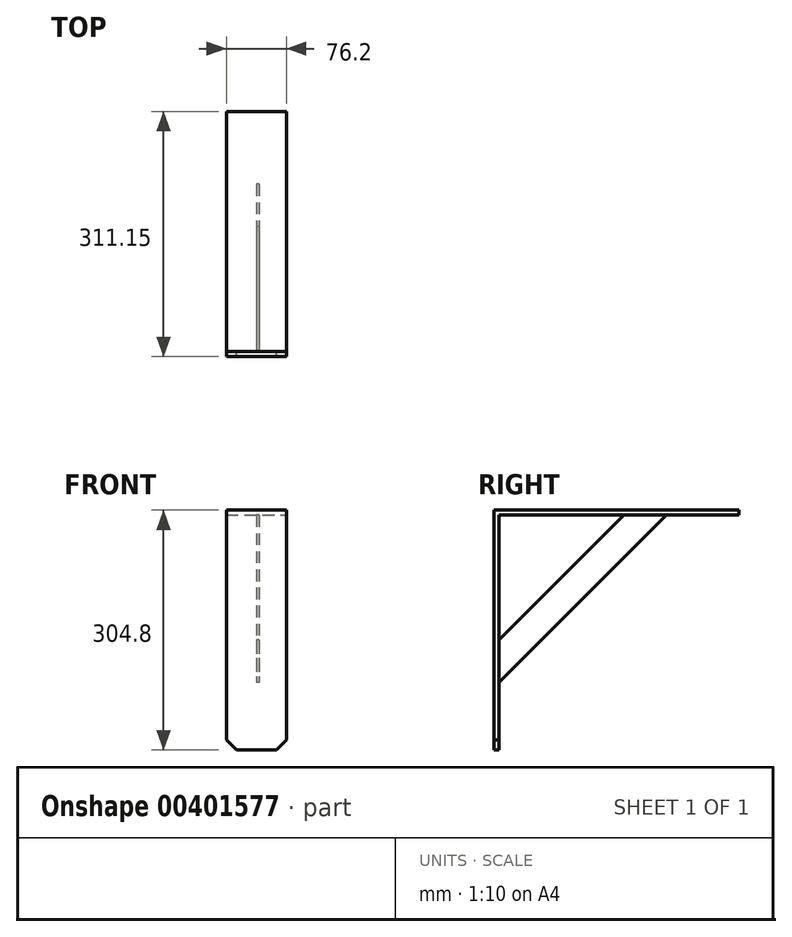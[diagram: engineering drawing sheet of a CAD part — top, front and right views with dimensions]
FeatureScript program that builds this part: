
annotation { "Feature Type Name" : "Feature", "Feature Type Description" : "" }
export const myFeature = defineFeature(function(context is Context, id is Id, definition is map)
    precondition{}
    {
        {
            var Q0;
            Q0=qCreatedBy(makeId("Front.planeOp"),FACE);
            var sketch = newSketch(context, id + "F0", { "sketchPlane" : qUnion([Q0])});
            skLineSegment(sketch, "E0.bottom", {"start": v(25.4, -152.4) * mm, "end": v(-38.1, -152.4) * mm});
            skLineSegment(sketch, "E0.top", {"start": v(38.1, 152.4) * mm, "end": v(-38.1, 152.4) * mm});
            skLineSegment(sketch, "E0.left", {"start": v(38.1, -139.7) * mm, "end": v(38.1, 152.4) * mm});
            skLineSegment(sketch, "E0.right", {"start": v(-38.1, -139.7) * mm, "end": v(-38.1, 152.4) * mm});
            skPoint(sketch, "E0.middle", {"position": v(0, 0) * mm});
            skLineSegment(sketch, "E1", {"start": v(-38.1, -139.7) * mm, "end": v(-25.4, -152.4) * mm});
            skLineSegment(sketch, "E2", {"start": v(25.4, -152.4) * mm, "end": v(38.1, -139.7) * mm});
            skPoint(sketch, "E3.orphan", {"position": v(38.1, -152.4) * mm});
            skSolve(sketch);
        }
        {
            var Q0;
            Q0=makeQuery(id+"F0.imprint","IMPRINT",FACE,{"disambiguationData":[TD([[makeQuery(id+"F0.imprint","IMPRINT",EDGE,{"derivedFrom":sQuery(id+"F0.wireOp",EDGE,"E0.bottom")}),-1.0]])]});
            extrude(context, id + "F1", {"entities" : qUnion([Q0]), "depth" : 6.35 * mm});
        }
        {
            var Q0;
            Q0=qCreatedBy(makeId("Right.planeOp"),FACE);
            cPlane(context, id + "F2", {"entities" : qUnion([Q0]), "cplaneType" : CPlaneType.OFFSET, "offset" : 38.1 * mm, "width" : 152.4 * mm, "height" : 152.4 * mm});
        }
        {
            var Q0;
            Q0=qCreatedBy(id+"F2.planeOp",FACE);
            var sketch = newSketch(context, id + "F3", { "sketchPlane" : qUnion([Q0])});
            skLineSegment(sketch, "E4.bottom", {"start": v(0, 152.26) * mm, "end": v(304.8, 152.26) * mm});
            skLineSegment(sketch, "E4.top", {"start": v(0, 145.91) * mm, "end": v(304.8, 145.91) * mm});
            skLineSegment(sketch, "E4.left", {"start": v(0, 152.26) * mm, "end": v(0, 145.91) * mm});
            skLineSegment(sketch, "E4.right", {"start": v(304.8, 152.26) * mm, "end": v(304.8, 145.91) * mm});
            skSolve(sketch);
        }
        {
            var Q0;
            Q0=makeQuery(id+"F3.imprint","IMPRINT",FACE,{"disambiguationData":[TD([[makeQuery(id+"F3.imprint","IMPRINT",EDGE,{"derivedFrom":sQuery(id+"F3.wireOp",EDGE,"E4.bottom")}),-1.0]])]});
            extrude(context, id + "F4", {"entities" : qUnion([Q0]), "operationType" : NewBodyOperationType.ADD, "oppositeDirection" : true, "depth" : 76.2 * mm});
        }
        {
            var Q0;
            Q0=qCreatedBy(makeId("Right.planeOp"),FACE);
            var sketch = newSketch(context, id + "F5", { "sketchPlane" : qUnion([Q0])});
            skLineSegment(sketch, "E5", {"start": v(212.56, 145.91) * mm, "end": v(0, -66.65) * mm});
            skLineSegment(sketch, "E6", {"start": v(158.68, 145.91) * mm, "end": v(0, -12.77) * mm});
            skLineSegment(sketch, "E7", {"start": v(212.56, 145.91) * mm, "end": v(158.68, 145.91) * mm});
            skLineSegment(sketch, "E8", {"start": v(0, -12.77) * mm, "end": v(0, -66.65) * mm});
            skPoint(sketch, "E9", {"position": v(215.9, 145.66) * mm});
            skPoint(sketch, "E10", {"position": v(0, -63.5) * mm});
            skSolve(sketch);
        }
        {
            var Q0;
            Q0=makeQuery(id+"F5.imprint","IMPRINT",FACE,{"disambiguationData":[TD([[makeQuery(id+"F5.imprint","IMPRINT",EDGE,{"derivedFrom":sQuery(id+"F5.wireOp",EDGE,"E5")}),-1.0]])]});
            extrude(context, id + "F6", {"entities" : qUnion([Q0]), "operationType" : NewBodyOperationType.ADD, "depth" : 3.17 * mm});
        }
        {
            var Q0;
            Q0=qSketchRegion(id+"F5",true);
            extrude(context, id + "F7", {"entities" : qUnion([Q0]), "operationType" : NewBodyOperationType.ADD, "depth" : 3.17 * mm});
        }
    });
